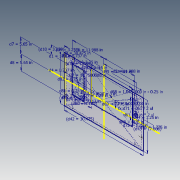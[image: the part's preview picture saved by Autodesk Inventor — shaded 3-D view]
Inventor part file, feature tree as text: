
AUTODESK INVENTOR PART (.ipt)
format: ipt  version: 2020.3 (Build 243373000, 373)  size: 244,736 bytes
history: native  units: in
note: dims shown in document units (in); Inventor stores cm internally (conversion verified against a paired STEP export)
features: extrude x5, sketch x4, hole x4, fillet x3
ambient origin geometry x8: Origin, YZ Plane, XZ Plane, XY Plane, X Axis, Y Axis, Z Axis, Center Point
bodies: Solid1 (feature_tree)
feature tree (16):
  sketch  "Sketch1"  dims[d0=30.475in d1=17.8in]
  extrude  "Extrusion1"  Depth=17.8in
  hole  "Hole1-M6 Clearance"  [1 undecoded]
  extrude  "Extrusion2"  Depth=11.988in
  hole  "Hole2-Tap M5"  [1 undecoded]
  fillet  "Fillet1"  Radius=3.2495in
  sketch  "Sketch4"  dims[d5=11.988in d6=11.988in]
  extrude  "Extrusion3"  Depth=0.125in
  hole  "Hole3-Tap M5"  [1 undecoded]
  fillet  "Fillet2"  Radius=3.0in
  sketch  "Sketch5"  dims[d7=5.65in d8=5.65in d9=3.2495in d10=3.25in d11=0.25in d12=0.0in d13=0.3125in d14=0.75in d15=0.375in d16=0.25in d17=0.5635in d18=1.0in d19=0.8108in d20=3.0in d23=16.0in d24=1.0in d25=0.0in d26=0.0in d27=11.75in d28=3.25in d29=1.1024in d30=1.1024in d31=6.181in d32=0.16in d33=0.75in d34=0.375in d35=0.25in d36=0.5635in d37=1.0in d38=0.8108in d39=0.75in d40=0.75in d41=0.25in d42=30.475in d43=17.8in d44=8.0453in d48=0.25in d50=1.0in d51=0.0in d52=0.16in d53=0.75in d54=0.375in d55=0.25in d56=0.5635in d57=1.0in d58=0.8108in d61=8.0in d64=0.125in d68=0.7937in d69=2.775in d71=4.0in d72=1.25in d73=8.0in d74=4.5in d75=10.25in d76=10.12in d77=1.25in d78=1.788in d79=5.1175in d80=5.12in d81=0.25in d82=0.25in d83=0.75in d84=0.1628in d85=0.394in d86=0.37in d87=0.25in d88=90.0deg d89=0.559in d90=0.8108in d91=0.0in d92=0.0in d93=0.125in d94=1.25in d95=12.469in d96=1.775in d97=0.0in d98=0.0in]
  hole  "Hole4"  [1 undecoded]
  extrude  "Extrusion4"  Depth=0.125in TaperAngle=0.0deg
  fillet  "Fillet3"  [1 undecoded]
  extrude  "Extrusion5"  Depth=11.75in
  sketch  "Sketch3"  dims[d3=0.737in d4=0.737in]
note: 5 required parameter values undecoded (feature->parameter linkage not recoverable at this tier; creation-order binding heuristic only, values carry confidence <= 0.55)
